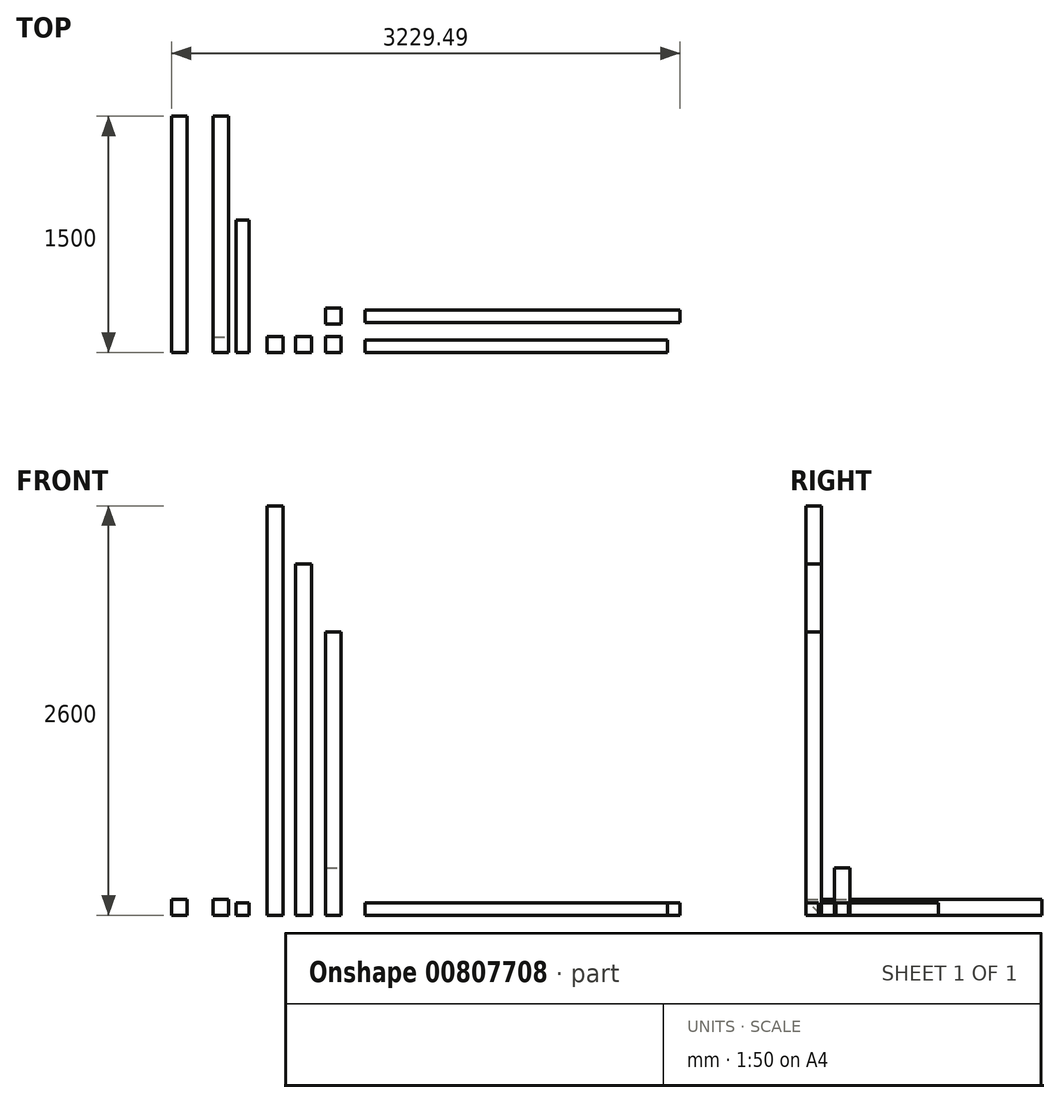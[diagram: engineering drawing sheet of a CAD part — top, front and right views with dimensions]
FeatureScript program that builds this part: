
annotation { "Feature Type Name" : "Feature", "Feature Type Description" : "" }
export const myFeature = defineFeature(function(context is Context, id is Id, definition is map)
    precondition{}
    {
        {
            var Q0;
            Q0=qCreatedBy(makeId("Top.planeOp"),FACE);
            var sketch = newSketch(context, id + "F0", { "sketchPlane" : qUnion([Q0])});
            skLineSegment(sketch, "E0.bottom", {"start": v(-196.1, 112.34) * mm, "end": v(-96.1, 112.34) * mm});
            skLineSegment(sketch, "E0.top", {"start": v(-196.1, 12.34) * mm, "end": v(-96.1, 12.34) * mm});
            skLineSegment(sketch, "E0.left", {"start": v(-196.1, 112.34) * mm, "end": v(-196.1, 12.34) * mm});
            skLineSegment(sketch, "E0.right", {"start": v(-96.1, 112.34) * mm, "end": v(-96.1, 12.34) * mm});
            skLineSegment(sketch, "E1.bottom", {"start": v(-440.87, 12.34) * mm, "end": v(-540.87, 12.34) * mm});
            skLineSegment(sketch, "E1.top", {"start": v(-440.87, 1512.34) * mm, "end": v(-540.87, 1512.34) * mm});
            skLineSegment(sketch, "E1.left", {"start": v(-440.87, 12.34) * mm, "end": v(-440.87, 1512.34) * mm});
            skLineSegment(sketch, "E1.right", {"start": v(-540.87, 12.34) * mm, "end": v(-540.87, 1512.34) * mm});
            skLineSegment(sketch, "E2.bottom", {"start": v(424.93, 12.34) * mm, "end": v(2344.93, 12.34) * mm});
            skLineSegment(sketch, "E2.top", {"start": v(424.93, 92.34) * mm, "end": v(2344.93, 92.34) * mm});
            skLineSegment(sketch, "E2.left", {"start": v(424.93, 12.34) * mm, "end": v(424.93, 92.34) * mm});
            skLineSegment(sketch, "E2.right", {"start": v(2344.93, 12.34) * mm, "end": v(2344.93, 92.34) * mm});
            skLineSegment(sketch, "E3.bottom", {"start": v(424.93, 202.52) * mm, "end": v(2424.93, 202.52) * mm});
            skLineSegment(sketch, "E3.top", {"start": v(424.93, 282.52) * mm, "end": v(2424.93, 282.52) * mm});
            skLineSegment(sketch, "E3.left", {"start": v(424.93, 202.52) * mm, "end": v(424.93, 282.52) * mm});
            skLineSegment(sketch, "E3.right", {"start": v(2424.93, 202.52) * mm, "end": v(2424.93, 282.52) * mm});
            skLineSegment(sketch, "E4.bottom", {"start": v(-393.1, 12.34) * mm, "end": v(-313.1, 12.34) * mm});
            skLineSegment(sketch, "E4.top", {"start": v(-393.1, 852.34) * mm, "end": v(-313.1, 852.34) * mm});
            skLineSegment(sketch, "E4.left", {"start": v(-393.1, 12.34) * mm, "end": v(-393.1, 852.34) * mm});
            skLineSegment(sketch, "E4.right", {"start": v(-313.1, 12.34) * mm, "end": v(-313.1, 852.34) * mm});
            skLineSegment(sketch, "E5.bottom", {"start": v(-704.56, 12.34) * mm, "end": v(-804.56, 12.34) * mm});
            skLineSegment(sketch, "E5.top", {"start": v(-704.56, 1512.34) * mm, "end": v(-804.56, 1512.34) * mm});
            skLineSegment(sketch, "E5.left", {"start": v(-704.56, 12.34) * mm, "end": v(-704.56, 1512.34) * mm});
            skLineSegment(sketch, "E5.right", {"start": v(-804.56, 12.34) * mm, "end": v(-804.56, 1512.34) * mm});
            skLineSegment(sketch, "E6.bottom", {"start": v(-16.63, 12.34) * mm, "end": v(83.37, 12.34) * mm});
            skLineSegment(sketch, "E6.top", {"start": v(-16.63, 112.34) * mm, "end": v(83.37, 112.34) * mm});
            skLineSegment(sketch, "E6.left", {"start": v(-16.63, 12.34) * mm, "end": v(-16.63, 112.34) * mm});
            skLineSegment(sketch, "E6.right", {"start": v(83.37, 12.34) * mm, "end": v(83.37, 112.34) * mm});
            skLineSegment(sketch, "E7.bottom", {"start": v(172.8, 12.34) * mm, "end": v(272.8, 12.34) * mm});
            skLineSegment(sketch, "E7.top", {"start": v(172.8, 112.34) * mm, "end": v(272.8, 112.34) * mm});
            skLineSegment(sketch, "E7.left", {"start": v(172.8, 12.34) * mm, "end": v(172.8, 112.34) * mm});
            skLineSegment(sketch, "E7.right", {"start": v(272.8, 12.34) * mm, "end": v(272.8, 112.34) * mm});
            skLineSegment(sketch, "E8.bottom", {"start": v(172.8, 193.34) * mm, "end": v(272.8, 193.34) * mm});
            skLineSegment(sketch, "E8.top", {"start": v(172.8, 293.34) * mm, "end": v(272.8, 293.34) * mm});
            skLineSegment(sketch, "E8.left", {"start": v(172.8, 193.34) * mm, "end": v(172.8, 293.34) * mm});
            skLineSegment(sketch, "E8.right", {"start": v(272.8, 193.34) * mm, "end": v(272.8, 293.34) * mm});
            skSolve(sketch);
        }
        {
            var Q0;
            Q0=makeQuery(id+"F0.imprint","IMPRINT",FACE,{"disambiguationData":[TD([[makeQuery(id+"F0.imprint","IMPRINT",EDGE,{"derivedFrom":sQuery(id+"F0.wireOp",EDGE,"E0.bottom")}),-1.0]])]});
            extrude(context, id + "F1", {"entities" : qUnion([Q0]), "depth" : 2600 * mm, "offsetDistance" : 25 * mm});
        }
        {
            var Q0;
            Q0=makeQuery(id+"F0.imprint","IMPRINT",FACE,{"disambiguationData":[TD([[makeQuery(id+"F0.imprint","IMPRINT",EDGE,{"derivedFrom":sQuery(id+"F0.wireOp",EDGE,"E6.bottom")}),1.0]])]});
            extrude(context, id + "F2", {"entities" : qUnion([Q0]), "depth" : 2230 * mm, "offsetDistance" : 25 * mm});
        }
        {
            var Q0;
            Q0=makeQuery(id+"F0.imprint","IMPRINT",FACE,{"disambiguationData":[TD([[makeQuery(id+"F0.imprint","IMPRINT",EDGE,{"derivedFrom":sQuery(id+"F0.wireOp",EDGE,"E7.bottom")}),1.0]])]});
            extrude(context, id + "F3", {"entities" : qUnion([Q0]), "depth" : 1800 * mm, "offsetDistance" : 25 * mm});
        }
        {
            var Q0;
            Q0=makeQuery(id+"F0.imprint","IMPRINT",FACE,{"disambiguationData":[TD([[makeQuery(id+"F0.imprint","IMPRINT",EDGE,{"derivedFrom":sQuery(id+"F0.wireOp",EDGE,"E1.bottom")}),-1.0]])]});
            var Q1;
            Q1=makeQuery(id+"F0.imprint","IMPRINT",FACE,{"disambiguationData":[TD([[makeQuery(id+"F0.imprint","IMPRINT",EDGE,{"derivedFrom":sQuery(id+"F0.wireOp",EDGE,"E5.bottom")}),-1.0]])]});
            extrude(context, id + "F4", {"entities" : qUnion([Q0, Q1]), "depth" : 100 * mm, "offsetDistance" : 25 * mm});
        }
        {
            var Q0;
            Q0=makeQuery(id+"F0.imprint","IMPRINT",FACE,{"disambiguationData":[TD([[makeQuery(id+"F0.imprint","IMPRINT",EDGE,{"derivedFrom":sQuery(id+"F0.wireOp",EDGE,"E8.bottom")}),1.0]])]});
            extrude(context, id + "F5", {"entities" : qUnion([Q0]), "depth" : 300 * mm, "offsetDistance" : 25 * mm});
        }
        {
            var Q0;
            Q0=makeQuery(id+"F0.imprint","IMPRINT",FACE,{"disambiguationData":[TD([[makeQuery(id+"F0.imprint","IMPRINT",EDGE,{"derivedFrom":sQuery(id+"F0.wireOp",EDGE,"E2.bottom")}),1.0]])]});
            var Q1;
            Q1=makeQuery(id+"F0.imprint","IMPRINT",FACE,{"disambiguationData":[TD([[makeQuery(id+"F0.imprint","IMPRINT",EDGE,{"derivedFrom":sQuery(id+"F0.wireOp",EDGE,"E3.bottom")}),1.0]])]});
            var Q2;
            Q2=makeQuery(id+"F0.imprint","IMPRINT",FACE,{"disambiguationData":[TD([[makeQuery(id+"F0.imprint","IMPRINT",EDGE,{"derivedFrom":sQuery(id+"F0.wireOp",EDGE,"E4.bottom")}),1.0]])]});
            extrude(context, id + "F6", {"entities" : qUnion([Q0, Q1, Q2]), "depth" : 80 * mm, "offsetDistance" : 25 * mm});
        }
        {
            var Q0;
            Q0=makeQuery(id+"F4.opExtrude","SWEPT_FACE",FACE,{"disambiguationData":[OSD([sQuery(id+"F0.wireOp",EDGE,"E1.left")])]});
            var sketch = newSketch(context, id + "F7", { "sketchPlane" : qUnion([Q0])});
            skLineSegment(sketch, "E9", {"start": v(12.34, 97.1) * mm, "end": v(12.34, 0) * mm});
            skLineSegment(sketch, "E10", {"start": v(12.34, 0) * mm, "end": v(109.44, 0) * mm});
            skLineSegment(sketch, "E11", {"start": v(109.44, 0) * mm, "end": v(12.34, 100) * mm});
            skSolve(sketch);
        }
        {
            var Q0;
            {var subQ0=sQuery(id+"F7.wireOp",EDGE,"E9");Q0=makeQuery(id+"F7.imprint","IMPRINT",FACE,{"disambiguationData":[TD([[makeQuery(id+"F7.imprint","IMPRINT",EDGE,{"derivedFrom":subQ0}),1.0]])]});}
            extrude(context, id + "F8", {"entities" : qUnion([Q0]), "operationType" : NewBodyOperationType.REMOVE, "oppositeDirection" : true, "depth" : 100 * mm, "offsetDistance" : 25 * mm});
        }
    });
